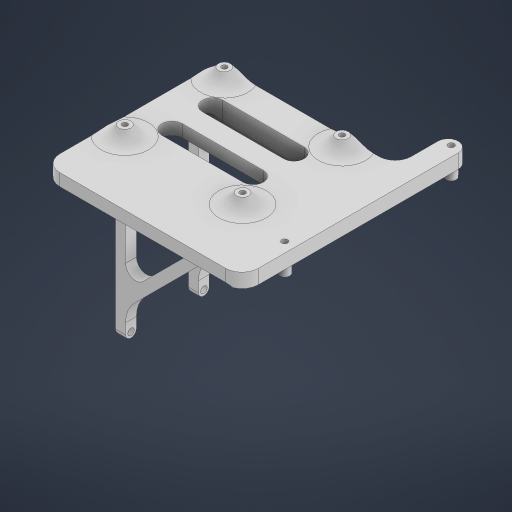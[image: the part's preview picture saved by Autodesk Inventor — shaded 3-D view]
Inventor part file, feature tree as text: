
AUTODESK INVENTOR PART (.ipt)
format: ipt  version: 2024.2 (Build 282272000, 272)  size: 1,335,808 bytes
history: native  units: mm
features: extrude x29, sketch x28, projected_geometry x23, fillet x11, other x1, chamfer x1
ambient origin geometry x8: Origin, YZ Plane, XZ Plane, XY Plane, X Axis, Y Axis, Z Axis, Center Point
bodies: Body1 (feature_tree)
feature tree (93):
  other  "솔리드1"
  extrude  "돌출1"  Depth=3.0mm
  extrude  "돌출2"  Depth=1.0mm
  extrude  "돌출4"  Depth=81.4mm TaperAngle=0.0deg
  extrude  "돌출5"  Depth=5.0mm
  extrude  "돌출6"  Depth=5.0mm
  extrude  "돌출7"  Depth=1.0mm
  extrude  "돌출8"  Depth=1.0mm TaperAngle=0.0deg
  extrude  "돌출9"  Depth=5.0mm
  extrude  "돌출10"  Depth=1.0mm
  extrude  "돌출11"  Depth=2.0mm TaperAngle=0.0deg
  extrude  "돌출12"  Depth=1.0mm TaperAngle=0.0deg
  extrude  "돌출13"  Depth=1.0mm TaperAngle=0.0deg
  extrude  "돌출14"  Depth=5.0mm
  fillet  "모깎기1"  Radius=1.0mm
  extrude  "돌출15"  Depth=1.0mm TaperAngle=0.0deg
  extrude  "돌출16"  Depth=1.0mm TaperAngle=0.0deg
  chamfer  "모따기1"  Distance=79.4mm
  extrude  "돌출17"  Depth=79.4mm TaperAngle=0.0deg
  fillet  "모깎기2"  Radius=10.0mm
  extrude  "돌출18"  Depth=1.0mm
  fillet  "모깎기4"  Radius=33.05mm
  extrude  "돌출19"  Depth=92.7mm TaperAngle=0.0deg
  extrude  "돌출20"  Depth=10.0mm
  extrude  "돌출21"  Depth=1.0mm
  sketch  "스케치23"
  extrude  "돌출22"  Depth=5.0mm TaperAngle=0.0deg
  extrude  "돌출23"  Depth=1.0mm TaperAngle=0.0deg
  sketch  "스케치24"
  extrude  "돌출24"  Depth=1.0mm
  extrude  "돌출26"  Depth=2.35mm
  extrude  "돌출27"  Depth=5.3mm
  fillet  "모깎기5"  Radius=85.05mm
  fillet  "모깎기6"  Radius=3.3mm
  fillet  "모깎기7"  Radius=2.65mm
  extrude  "돌출28"  Depth=2.65mm
  extrude  "돌출29"  Depth=85.05mm TaperAngle=0.0deg
  extrude  "돌출30"  Depth=2.65mm
  extrude  "돌출31"  Depth=10.0mm
  fillet  "모깎기8"  Radius=1.0mm
  fillet  "모깎기9"  Radius=25.9mm
  fillet  "모깎기10"  Radius=1.0mm
  fillet  "모깎기11"  Radius=5.3mm
  fillet  "모깎기12"  Radius=10.0mm
  sketch  "스케치1"
  sketch  "스케치2"
  projected_geometry  "투영된 루프1"
  sketch  "스케치4"
  sketch  "스케치6"
  projected_geometry  "투영된 루프2"
  sketch  "스케치7"
  projected_geometry  "투영된 루프3"
  sketch  "스케치8"
  sketch  "스케치9"
  projected_geometry  "투영된 루프4"
  projected_geometry  "투영된 루프5"
  sketch  "스케치10"
  sketch  "스케치11"
  sketch  "스케치12"
  sketch  "스케치13"
  projected_geometry  "투영된 루프6"
  projected_geometry  "투영된 루프7"
  sketch  "스케치14"
  sketch  "스케치15"
  sketch  "스케치16"
  projected_geometry  "투영된 루프8"
  sketch  "스케치17"
  projected_geometry  "투영된 루프9"
  sketch  "스케치18"
  projected_geometry  "투영된 루프10"
  sketch  "스케치19"
  sketch  "스케치20"
  sketch  "스케치21"
  sketch  "스케치22"
  projected_geometry  "투영된 루프11"
  projected_geometry  "투영된 루프12"
  projected_geometry  "투영된 루프13"
  projected_geometry  "투영된 루프14"
  projected_geometry  "투영된 루프15"
  sketch  "스케치25"
  projected_geometry  "투영된 루프16"
  projected_geometry  "투영된 루프17"
  sketch  "스케치26"
  projected_geometry  "투영된 루프18"
  projected_geometry  "투영된 루프19"
  sketch  "스케치27"
  projected_geometry  "투영된 루프20"
  sketch  "스케치28"
  projected_geometry  "투영된 루프21"
  sketch  "스케치29"
  projected_geometry  "투영된 루프22"
  sketch  "스케치30"
  projected_geometry  "투영된 루프23"
